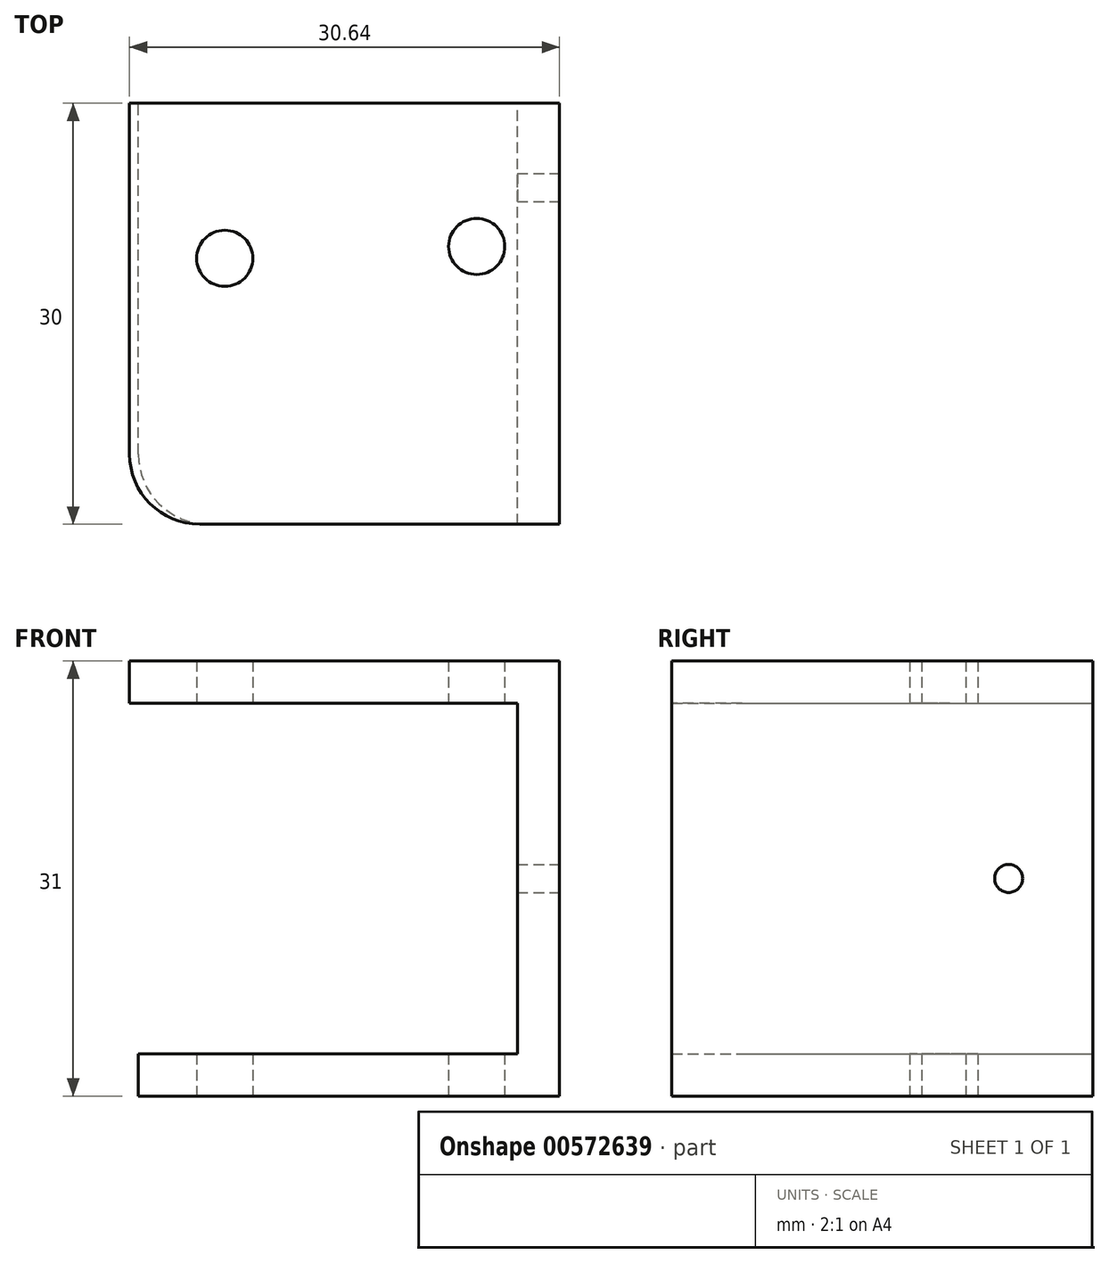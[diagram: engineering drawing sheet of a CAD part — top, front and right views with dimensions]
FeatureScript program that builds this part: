
annotation { "Feature Type Name" : "Feature", "Feature Type Description" : "" }
export const myFeature = defineFeature(function(context is Context, id is Id, definition is map)
    precondition{}
    {
        {
            var Q0;
            Q0=qCreatedBy(makeId("Front.planeOp"),FACE);
            var sketch = newSketch(context, id + "F0", { "sketchPlane" : qUnion([Q0])});
            skLineSegment(sketch, "E0", {"start": v(-25.76, -19.93) * mm, "end": v(4.24, -19.93) * mm});
            skLineSegment(sketch, "E1", {"start": v(4.24, -19.93) * mm, "end": v(4.24, 11.07) * mm});
            skLineSegment(sketch, "E2", {"start": v(4.24, 11.07) * mm, "end": v(-26.4, 11.07) * mm});
            skLineSegment(sketch, "E3", {"start": v(-26.4, 11.07) * mm, "end": v(-26.4, 8.07) * mm});
            skLineSegment(sketch, "E4", {"start": v(-26.4, 8.07) * mm, "end": v(1.24, 8.07) * mm});
            skLineSegment(sketch, "E5", {"start": v(1.24, 8.07) * mm, "end": v(1.24, -16.93) * mm});
            skLineSegment(sketch, "E6", {"start": v(1.24, -16.93) * mm, "end": v(-25.76, -16.93) * mm});
            skLineSegment(sketch, "E7", {"start": v(-25.76, -16.93) * mm, "end": v(-25.76, -19.93) * mm});
            skSolve(sketch);
        }
        {
            var Q0;
            Q0 = qSketchRegion(id + "F0", true);
            extrude(context, id + "F1", {"entities" : qUnion([Q0]), "depth" : 30 * mm, "offsetDistance" : 25.4 * mm});
        }
        {
            var Q0;
            Q0=makeQuery(id+"F1.opExtrude","SWEPT_FACE",FACE,{"disambiguationData":[OSD([sQuery(id+"F0.wireOp",EDGE,"E1")])]});
            var sketch = newSketch(context, id + "F2", { "sketchPlane" : qUnion([Q0])});
            skPoint(sketch, "E8", {"position": v(-6, -4.43) * mm});
            skPoint(sketch, "E8.positionSnap0", {"position": v(0, -4.43) * mm});
            skSolve(sketch);
        }
        {
            var Q0;
            Q0=sQuery(id+"F2.wireOp",VERTEX,"E8");
            var Q1;
            Q1=makeQuery(id+"F1.opExtrude","SWEPT_BODY",BODY,{"disambiguationData":[OSD([sQuery(id+"F0.wireOp",EDGE,"E0"),sQuery(id+"F0.wireOp",EDGE,"E1"),sQuery(id+"F0.wireOp",EDGE,"E2"),sQuery(id+"F0.wireOp",EDGE,"E3"),sQuery(id+"F0.wireOp",EDGE,"E4"),sQuery(id+"F0.wireOp",EDGE,"E5"),sQuery(id+"F0.wireOp",EDGE,"E6"),sQuery(id+"F0.wireOp",EDGE,"E7")])]});
            hole(context, id + "F3", {"style" : HoleStyle.SIMPLE, "endStyle" : HoleEndStyle.THROUGH, "holeDiameter" : 2 * mm, "isTappedThrough" : true, "tappedDepth" : 12 * mm, "tapClearance" : 3, "locations" : qUnion([Q0]), "scope" : qUnion([Q1])});
        }
        {
            var Q0;
            Q0=makeQuery(id+"F1.opExtrude","SWEPT_FACE",FACE,{"disambiguationData":[OSD([sQuery(id+"F0.wireOp",EDGE,"E0")])]});
            var sketch = newSketch(context, id + "F4", { "sketchPlane" : qUnion([Q0])});
            skPoint(sketch, "E9", {"position": v(-1.66, 10.2) * mm});
            skPoint(sketch, "E10", {"position": v(-19.6, 11.05) * mm});
            skSolve(sketch);
        }
        {
            var Q0;
            Q0=sQuery(id+"F4.wireOp",VERTEX,"E10");
            var Q1;
            Q1=sQuery(id+"F4.wireOp",VERTEX,"E9");
            var Q2;
            Q2=makeQuery(id+"F1.opExtrude","SWEPT_BODY",BODY,{"disambiguationData":[OSD([sQuery(id+"F0.wireOp",EDGE,"E0"),sQuery(id+"F0.wireOp",EDGE,"E1"),sQuery(id+"F0.wireOp",EDGE,"E2"),sQuery(id+"F0.wireOp",EDGE,"E3"),sQuery(id+"F0.wireOp",EDGE,"E4"),sQuery(id+"F0.wireOp",EDGE,"E5"),sQuery(id+"F0.wireOp",EDGE,"E6"),sQuery(id+"F0.wireOp",EDGE,"E7")])]});
            hole(context, id + "F5", {"style" : HoleStyle.SIMPLE, "endStyle" : HoleEndStyle.THROUGH, "holeDiameter" : 4 * mm, "isTappedThrough" : true, "tappedDepth" : 12 * mm, "tapClearance" : 3, "locations" : qUnion([Q0, Q1]), "scope" : qUnion([Q2])});
        }
        {
            var Q0;
            Q0=makeQuery(id+"F1.opExtrude","CAP_EDGE",EDGE,{"disambiguationData":[OSD([sQuery(id+"F0.wireOp",EDGE,"E3")])],"isStart":false});
            fillet(context, id + "F6", {"entities" : qUnion([Q0]), "radius" : 5 * mm, "tangentPropagation" : true, "allowEdgeOverflow" : false});
        }
        {
            var Q0;
            Q0=makeQuery(id+"F1.opExtrude","CAP_EDGE",EDGE,{"disambiguationData":[OSD([sQuery(id+"F0.wireOp",EDGE,"E7")])],"isStart":false});
            fillet(context, id + "F7", {"entities" : qUnion([Q0]), "radius" : 5 * mm, "tangentPropagation" : true, "allowEdgeOverflow" : false});
        }
    });
